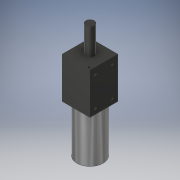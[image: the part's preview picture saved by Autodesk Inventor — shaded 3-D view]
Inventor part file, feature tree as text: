
AUTODESK INVENTOR PART (.ipt)
format: ipt  version: 2017 SP1 (Build 210196100, 196)  size: 138,240 bytes
history: native  units: in
note: dims shown in document units (in); Inventor stores cm internally (conversion verified against a paired STEP export)
features: extrude x5, sketch x5
ambient origin geometry x8: Origin, YZ Plane, XZ Plane, XY Plane, X Axis, Y Axis, Z Axis, Center Point
bodies: Solid1 (feature_tree)
feature tree (10):
  extrude  "Extrusion1"  Depth=1.65in
  extrude  "Extrusion2"  Depth=2.45in TaperAngle=0.0deg
  extrude  "Extrusion3"  Depth=2.8in TaperAngle=0.0deg
  extrude  "Extrusion4"  Depth=0.06in TaperAngle=0.0deg
  extrude  "Extrusion5"  Depth=1.6in TaperAngle=0.0deg
  sketch  "Sketch1"  dims[d0=1.65in d1=1.375in]
  sketch  "Sketch2"  dims[d2=0.2in d3=2.45in d4=0.0in]
  sketch  "Sketch3"  dims[d5=1.56in d6=2.8in d7=0.0in]
  sketch  "Sketch4"  dims[d8=0.5in d9=0.06in d10=0.0in]
  sketch  "Sketch5"  dims[d11=0.5in d12=1.6in d13=0.0in d14=1.0in d15=1.75in d16=0.4in d17=0.15in d18=1.6in d19=0.0in]
